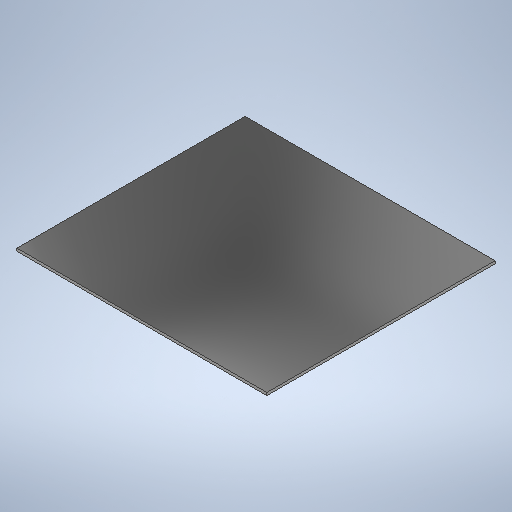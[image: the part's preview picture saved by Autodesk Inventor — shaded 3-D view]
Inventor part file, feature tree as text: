
AUTODESK INVENTOR PART (.ipt)
format: ipt  version: 2025 (Build 290162000, 162)  size: 245,248 bytes
history: native  units: in
note: dims shown in document units (in); Inventor stores cm internally (conversion verified against a paired STEP export)
features: extrude x1
ambient origin geometry x8: Origin, YZ Plane, XZ Plane, XY Plane, X Axis, Y Axis, Z Axis, Center Point
bodies: Solid1 (feature_tree)
feature tree (1):
  extrude  "Extrusion1"  Depth=0.8268in
